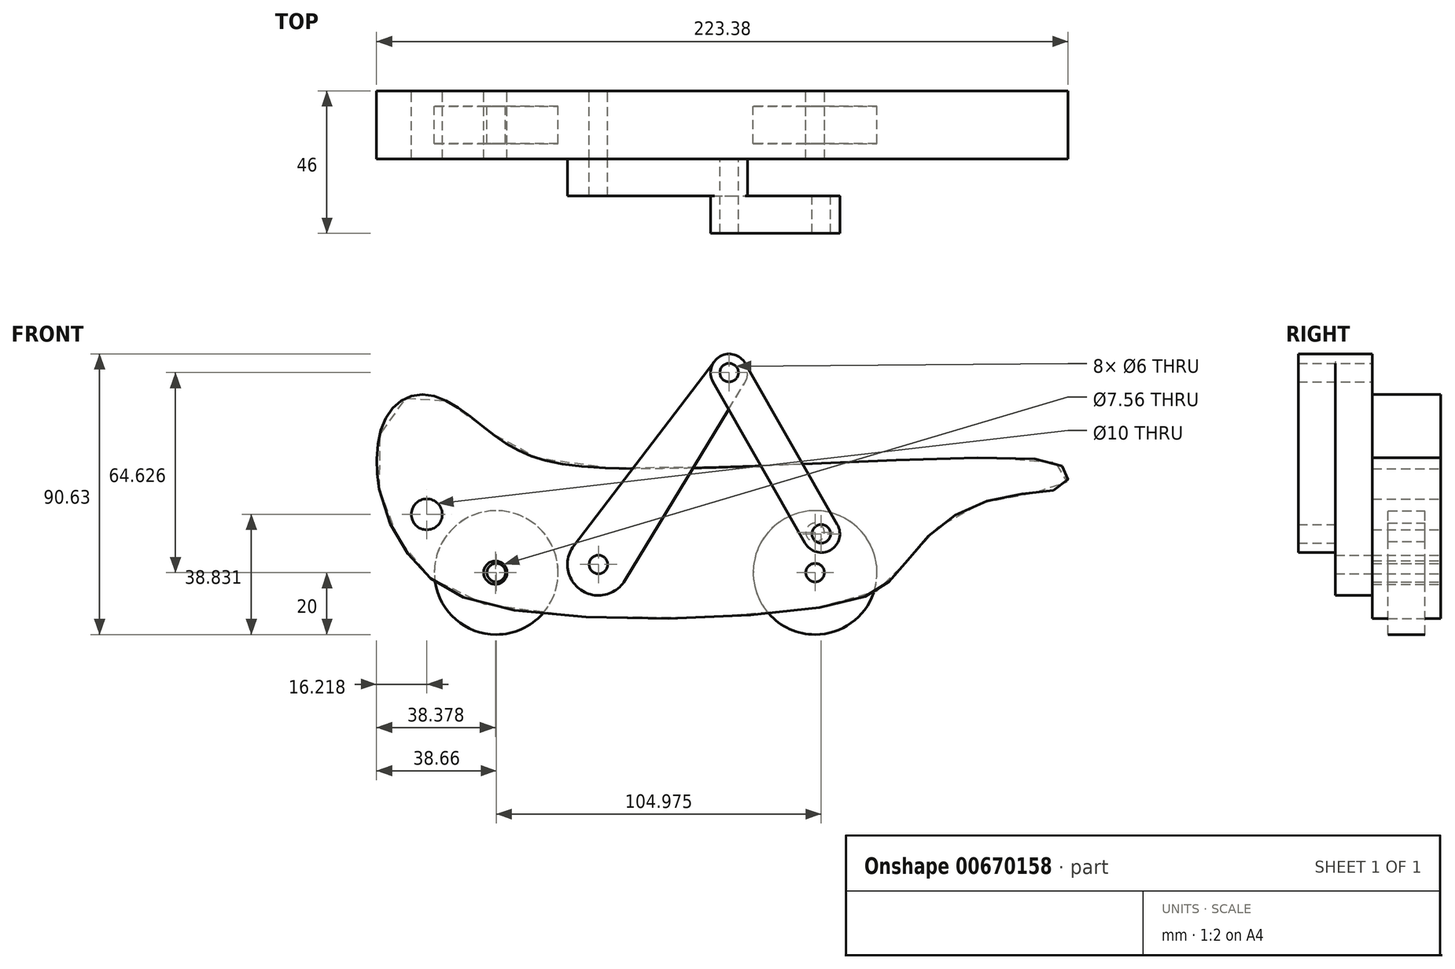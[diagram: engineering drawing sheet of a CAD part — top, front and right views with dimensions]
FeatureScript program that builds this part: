
annotation { "Feature Type Name" : "Feature", "Feature Type Description" : "" }
export const myFeature = defineFeature(function(context is Context, id is Id, definition is map)
    precondition{}
    {
        {
            var Q0;
            Q0=qCreatedBy(makeId("Front.planeOp"),FACE);
            var sketch = newSketch(context, id + "F0", { "sketchPlane" : qUnion([Q0])});
            skCircle(sketch, "E0", {"center": v(0, 0) * mm, "radius": 20 * mm});
            skCircle(sketch, "E1", {"center": v(0, 0) * mm, "radius": 3 * mm});
            skCircle(sketch, "E2", {"center": v(0, 13) * mm, "radius": 3 * mm});
            skSolve(sketch);
        }
        {
            var Q0;
            Q0 = qSketchRegion(id + "F0", true);
            extrude(context, id + "F1", {"entities" : qUnion([Q0]), "depth" : 6 * mm, "offsetDistance" : 25 * mm, "hasSecondDirection" : true, "secondDirectionOppositeDirection" : true, "secondDirectionDepth" : 6 * mm});
        }
        {
            var Q0;
            Q0=qCreatedBy(makeId("Front.planeOp"),FACE);
            var sketch = newSketch(context, id + "F2", { "sketchPlane" : qUnion([Q0])});
            skCircle(sketch, "E3", {"center": v(-103, 0) * mm, "radius": 20 * mm});
            skCircle(sketch, "E4", {"center": v(-103, 0) * mm, "radius": 3 * mm});
            skSolve(sketch);
        }
        {
            var Q0;
            Q0 = qSketchRegion(id + "F2", true);
            extrude(context, id + "F3", {"entities" : qUnion([Q0]), "depth" : 6 * mm, "offsetDistance" : 25 * mm, "hasSecondDirection" : true, "secondDirectionOppositeDirection" : true, "secondDirectionDepth" : 6 * mm});
        }
        {
            var Q0;
            Q0=qCreatedBy(makeId("Front.planeOp"),FACE);
            var sketch = newSketch(context, id + "F4", { "sketchPlane" : qUnion([Q0])});
            skFitSpline(sketch, "E5", {"points": [v(-140.84, 26.97) * mm, v(-129.82, 3.92) * mm, v(-100.88, -11.48) * mm, v(9.99, -9.64) * mm, v(26.6, 0) * mm, v(40.66, 15.48) * mm, v(63.5, 24.95) * mm, v(80.58, 28.17) * mm, v(81.32, 32.64) * mm, v(70.13, 36.75) * mm, v(-66.4, 33.76) * mm, v(-101.89, 43.1) * mm, v(-123.77, 57.24) * mm, v(-137.6, 51.7) * mm, v(-140.84, 26.97) * mm]});
            skCircle(sketch, "E6", {"center": v(-103.28, 0) * mm, "radius": 3.78 * mm});
            skCircle(sketch, "E7", {"center": v(-70, 2.64) * mm, "radius": 3 * mm});
            skCircle(sketch, "E8", {"center": v(0, 0) * mm, "radius": 3 * mm});
            skCircle(sketch, "E9", {"center": v(-125.44, 18.83) * mm, "radius": 5 * mm});
            skSolve(sketch);
        }
        {
            var Q0;
            Q0 = qSketchRegion(id + "F4", true);
            extrude(context, id + "F5", {"entities" : qUnion([Q0]), "depth" : 11 * mm, "offsetDistance" : 25 * mm, "hasSecondDirection" : true, "secondDirectionOppositeDirection" : true, "secondDirectionDepth" : 11 * mm});
        }
        {
            var Q0;
            Q0=makeQuery(id+"F5.opExtrude","CAP_FACE",FACE,{"disambiguationData":[OSD([sQuery(id+"F4.wireOp",EDGE,"E5"),sQuery(id+"F4.wireOp",EDGE,"E6"),sQuery(id+"F4.wireOp",EDGE,"EQEvsMUm-2aj1-pbCM-Zlr4-22iBlG7awbs4"),sQuery(id+"F4.wireOp",EDGE,"E7")])],"isStart":false});
            var sketch = newSketch(context, id + "F6", { "sketchPlane" : qUnion([Q0])});
            skCircle(sketch, "E10", {"center": v(-70, 2.64) * mm, "radius": 10 * mm});
            skCircle(sketch, "E11", {"center": v(-27.77, 64.63) * mm, "radius": 3 * mm});
            skCircle(sketch, "E12", {"center": v(-27.77, 64.63) * mm, "radius": 6 * mm});
            skLineSegment(sketch, "E13", {"start": v(-77.95, 8.7) * mm, "end": v(-32.54, 68.26) * mm});
            skLineSegment(sketch, "E14", {"start": v(-61.44, -2.54) * mm, "end": v(-22.64, 61.52) * mm});
            skCircle(sketch, "E15", {"center": v(-70, 2.64) * mm, "radius": 3 * mm});
            skSolve(sketch);
        }
        {
            var Q0;
            Q0 = qSketchRegion(id + "F6", true);
            extrude(context, id + "F7", {"entities" : qUnion([Q0]), "depth" : 12 * mm, "offsetDistance" : 25 * mm});
        }
        {
            var Q0;
            Q0=makeQuery(id+"F7.opExtrude","CAP_FACE",FACE,{"disambiguationData":[OSD([sQuery(id+"F6.wireOp",EDGE,"E10"),sQuery(id+"F6.wireOp",EDGE,"E11"),sQuery(id+"F6.wireOp",EDGE,"E12"),sQuery(id+"F6.wireOp",EDGE,"E13"),sQuery(id+"F6.wireOp",EDGE,"E14"),sQuery(id+"F6.wireOp",EDGE,"E15")])],"isStart":false});
            var sketch = newSketch(context, id + "F8", { "sketchPlane" : qUnion([Q0])});
            skCircle(sketch, "E16.0", {"center": v(-27.77, 64.63) * mm, "radius": 3 * mm});
            skCircle(sketch, "E17", {"center": v(-27.77, 64.63) * mm, "radius": 6 * mm});
            skCircle(sketch, "E18", {"center": v(1.97, 12.52) * mm, "radius": 3 * mm});
            skCircle(sketch, "E19", {"center": v(1.97, 12.52) * mm, "radius": 6 * mm});
            skLineSegment(sketch, "E20", {"start": v(-22.56, 67.6) * mm, "end": v(7.19, 15.5) * mm});
            skLineSegment(sketch, "E21", {"start": v(-32.98, 61.65) * mm, "end": v(-3.24, 9.54) * mm});
            skSolve(sketch);
        }
        {
            var Q0;
            Q0 = qSketchRegion(id + "F8", true);
            extrude(context, id + "F9", {"entities" : qUnion([Q0]), "operationType" : NewBodyOperationType.ADD, "depth" : 12 * mm, "offsetDistance" : 25 * mm});
        }
    });
